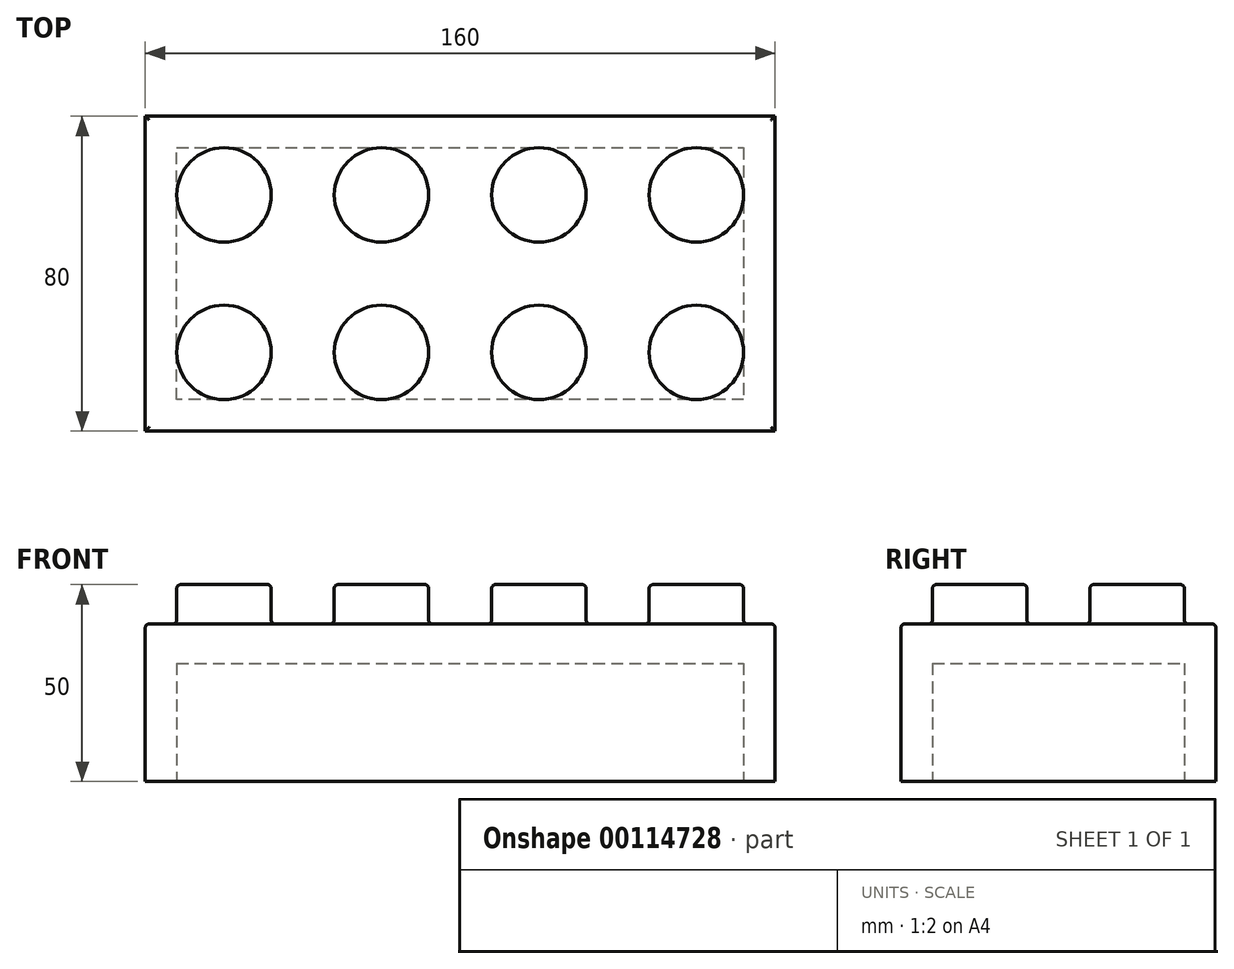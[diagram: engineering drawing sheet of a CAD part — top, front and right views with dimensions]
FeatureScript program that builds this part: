
annotation { "Feature Type Name" : "Feature", "Feature Type Description" : "" }
export const myFeature = defineFeature(function(context is Context, id is Id, definition is map)
    precondition{}
    {
        {
            var Q0;
            Q0=qCreatedBy(makeId("Top.planeOp"),FACE);
            var sketch = newSketch(context, id + "F0", { "sketchPlane" : qUnion([Q0])});
            skLineSegment(sketch, "E0.bottom", {"start": v(-81.33, 36.8) * mm, "end": v(78.67, 36.8) * mm});
            skLineSegment(sketch, "E0.top", {"start": v(-81.33, -43.2) * mm, "end": v(78.67, -43.2) * mm});
            skLineSegment(sketch, "E0.left", {"start": v(-81.33, 36.8) * mm, "end": v(-81.33, -43.2) * mm});
            skLineSegment(sketch, "E0.right", {"start": v(78.67, 36.8) * mm, "end": v(78.67, -43.2) * mm});
            skSolve(sketch);
        }
        {
            var Q0;
            Q0 = qSketchRegion(id + "F0", true);
            extrude(context, id + "F1", {"entities" : qUnion([Q0]), "depth" : 40 * mm});
        }
        {
            var Q0;
            Q0=makeQuery(id+"F1.opExtrude","CAP_FACE",FACE,{"disambiguationData":[OSD([sQuery(id+"F0.wireOp",EDGE,"E0.bottom"),sQuery(id+"F0.wireOp",EDGE,"E0.top"),sQuery(id+"F0.wireOp",EDGE,"E0.left"),sQuery(id+"F0.wireOp",EDGE,"E0.right")])],"isStart":true});
            var sketch = newSketch(context, id + "F2", { "sketchPlane" : qUnion([Q0])});
            skLineSegment(sketch, "E1.0", {"start": v(-73.33, -28.8) * mm, "end": v(70.67, -28.8) * mm});
            skLineSegment(sketch, "E1.1", {"start": v(-73.33, 35.2) * mm, "end": v(-73.33, -28.8) * mm});
            skLineSegment(sketch, "E1.2", {"start": v(70.67, 35.2) * mm, "end": v(-73.33, 35.2) * mm});
            skLineSegment(sketch, "E1.3", {"start": v(70.67, -28.8) * mm, "end": v(70.67, 35.2) * mm});
            skSolve(sketch);
        }
        {
            var Q0;
            Q0 = qSketchRegion(id + "F2", true);
            extrude(context, id + "F3", {"entities" : qUnion([Q0]), "operationType" : NewBodyOperationType.REMOVE, "oppositeDirection" : true, "depth" : 30 * mm});
        }
        {
            var Q0;
            Q0=makeQuery(id+"F1.opExtrude","CAP_FACE",FACE,{"disambiguationData":[OSD([sQuery(id+"F0.wireOp",EDGE,"E0.bottom"),sQuery(id+"F0.wireOp",EDGE,"E0.top"),sQuery(id+"F0.wireOp",EDGE,"E0.left"),sQuery(id+"F0.wireOp",EDGE,"E0.right")])],"isStart":false});
            var sketch = newSketch(context, id + "F4", { "sketchPlane" : qUnion([Q0])});
            skCircle(sketch, "E2", {"center": v(-61.33, 16.8) * mm, "radius": 12 * mm});
            skCircle(sketch, "E3.0.1.0", {"center": v(-61.33, -23.2) * mm, "radius": 12 * mm});
            skCircle(sketch, "E3.1.0.0", {"center": v(-21.33, 16.8) * mm, "radius": 12 * mm});
            skCircle(sketch, "E3.1.1.0", {"center": v(-21.33, -23.2) * mm, "radius": 12 * mm});
            skCircle(sketch, "E3.2.0.0", {"center": v(18.67, 16.8) * mm, "radius": 12 * mm});
            skCircle(sketch, "E3.2.1.0", {"center": v(18.67, -23.2) * mm, "radius": 12 * mm});
            skCircle(sketch, "E3.3.0.0", {"center": v(58.67, 16.8) * mm, "radius": 12 * mm});
            skCircle(sketch, "E3.3.1.0", {"center": v(58.67, -23.2) * mm, "radius": 12 * mm});
            skLineSegment(sketch, "E3.direction1", {"start": v(-61.33, 16.8) * mm, "end": v(-21.33, 16.8) * mm, "construction": true});
            skLineSegment(sketch, "E3.direction2", {"start": v(-61.33, 16.8) * mm, "end": v(-61.33, -23.2) * mm, "construction": true});
            skSolve(sketch);
        }
        {
            var Q0;
            Q0 = qSketchRegion(id + "F4", true);
            extrude(context, id + "F5", {"entities" : qUnion([Q0]), "operationType" : NewBodyOperationType.ADD, "depth" : 10 * mm});
        }
        {
            var Q0;
            Q0=makeQuery(id+"F5.opExtrude","CAP_FACE",FACE,{"disambiguationData":[OSD([sQuery(id+"F4.wireOp",EDGE,"E2")])],"isStart":false});
            var Q1;
            Q1=makeQuery(id+"F5.opExtrude","CAP_FACE",FACE,{"disambiguationData":[OSD([sQuery(id+"F4.wireOp",EDGE,"E3.1.0.0")])],"isStart":false});
            var Q2;
            Q2=makeQuery(id+"F5.opExtrude","CAP_FACE",FACE,{"disambiguationData":[OSD([sQuery(id+"F4.wireOp",EDGE,"E3.2.0.0")])],"isStart":false});
            var Q3;
            Q3=makeQuery(id+"F5.opExtrude","CAP_FACE",FACE,{"disambiguationData":[OSD([sQuery(id+"F4.wireOp",EDGE,"E3.3.0.0")])],"isStart":false});
            var Q4;
            Q4=makeQuery(id+"F5.opExtrude","CAP_FACE",FACE,{"disambiguationData":[OSD([sQuery(id+"F4.wireOp",EDGE,"E3.3.1.0")])],"isStart":false});
            var Q5;
            Q5=makeQuery(id+"F5.opExtrude","CAP_FACE",FACE,{"disambiguationData":[OSD([sQuery(id+"F4.wireOp",EDGE,"E3.2.1.0")])],"isStart":false});
            var Q6;
            Q6=makeQuery(id+"F5.opExtrude","CAP_FACE",FACE,{"disambiguationData":[OSD([sQuery(id+"F4.wireOp",EDGE,"E3.1.1.0")])],"isStart":false});
            var Q7;
            Q7=makeQuery(id+"F5.opExtrude","CAP_FACE",FACE,{"disambiguationData":[OSD([sQuery(id+"F4.wireOp",EDGE,"E3.0.1.0")])],"isStart":false});
            var Q8;
            Q8=makeQuery(id+"F1.opExtrude","CAP_FACE",FACE,{"disambiguationData":[OSD([sQuery(id+"F0.wireOp",EDGE,"E0.bottom"),sQuery(id+"F0.wireOp",EDGE,"E0.top"),sQuery(id+"F0.wireOp",EDGE,"E0.left"),sQuery(id+"F0.wireOp",EDGE,"E0.right")])],"isStart":false});
            fillet(context, id + "F6", {"entities" : qUnion([Q0, Q1, Q2, Q3, Q4, Q5, Q6, Q7, Q8]), "radius" : 1 * mm, "tangentPropagation" : true, "allowEdgeOverflow" : false});
        }
    });
